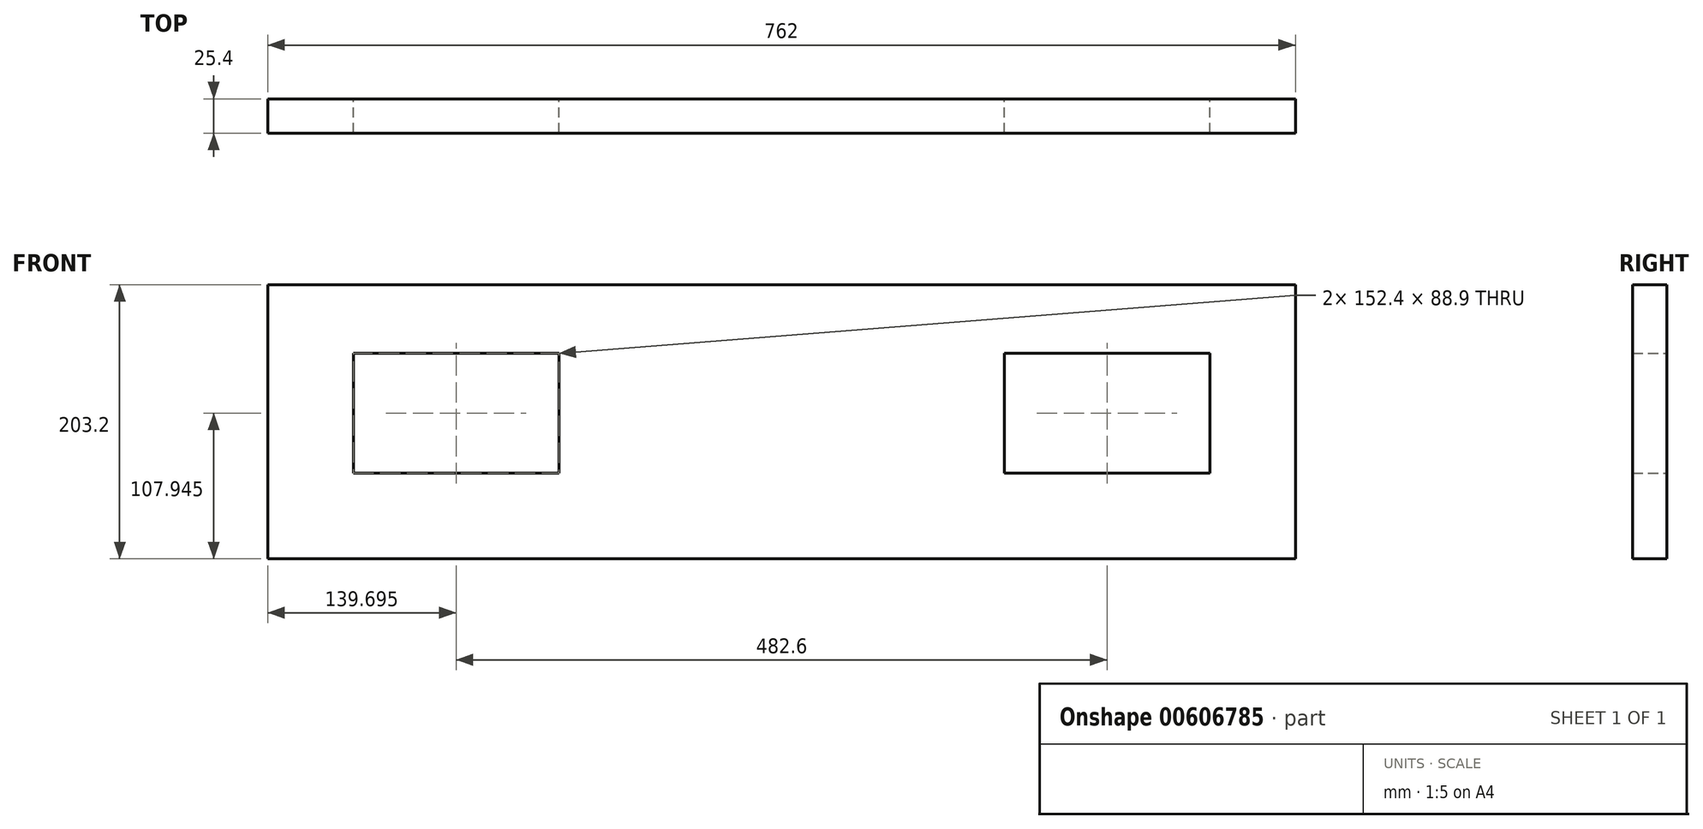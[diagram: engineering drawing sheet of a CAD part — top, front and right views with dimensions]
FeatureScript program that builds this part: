
annotation { "Feature Type Name" : "Feature", "Feature Type Description" : "" }
export const myFeature = defineFeature(function(context is Context, id is Id, definition is map)
    precondition{}
    {
        {
            var Q0;
            Q0=qCreatedBy(makeId("Front.planeOp"),FACE);
            var sketch = newSketch(context, id + "F0", { "sketchPlane" : qUnion([Q0])});
            skLineSegment(sketch, "E0.bottom", {"start": v(-437.36, -20.03) * mm, "end": v(324.64, -20.03) * mm});
            skLineSegment(sketch, "E0.top", {"start": v(-437.36, -223.23) * mm, "end": v(324.64, -223.23) * mm});
            skLineSegment(sketch, "E0.left", {"start": v(-437.36, -20.03) * mm, "end": v(-437.36, -223.23) * mm});
            skLineSegment(sketch, "E0.right", {"start": v(324.64, -20.03) * mm, "end": v(324.64, -223.23) * mm});
            skArc(sketch, "E1", {"start": v(19.28, -130.91) * mm, "mid": v(-58.16, -77.1) * mm, "end": v(-133.12, -134.33) * mm});
            skLineSegment(sketch, "E2", {"start": v(-133.12, -134.33) * mm, "end": v(19.28, -134.33) * mm});
            skLineSegment(sketch, "E3.bottom", {"start": v(-373.86, -70.83) * mm, "end": v(-221.46, -70.83) * mm});
            skLineSegment(sketch, "E3.top", {"start": v(-373.86, -159.73) * mm, "end": v(-221.46, -159.73) * mm});
            skLineSegment(sketch, "E3.left", {"start": v(-373.86, -70.83) * mm, "end": v(-373.86, -159.73) * mm});
            skLineSegment(sketch, "E3.right", {"start": v(-221.46, -70.83) * mm, "end": v(-221.46, -159.73) * mm});
            skLineSegment(sketch, "E4.bottom", {"start": v(108.74, -70.83) * mm, "end": v(261.14, -70.83) * mm});
            skLineSegment(sketch, "E4.top", {"start": v(108.74, -159.73) * mm, "end": v(261.14, -159.73) * mm});
            skLineSegment(sketch, "E4.left", {"start": v(108.74, -70.83) * mm, "end": v(108.74, -159.73) * mm});
            skLineSegment(sketch, "E4.right", {"start": v(261.14, -70.83) * mm, "end": v(261.14, -159.73) * mm});
            skSolve(sketch);
        }
        {
            var Q0;
            Q0 = qSketchRegion(id + "F0", true);
            extrude(context, id + "F1", {"entities" : qUnion([Q0]), "depth" : 25.4 * mm, "offsetDistance" : 25.4 * mm});
        }
    });
